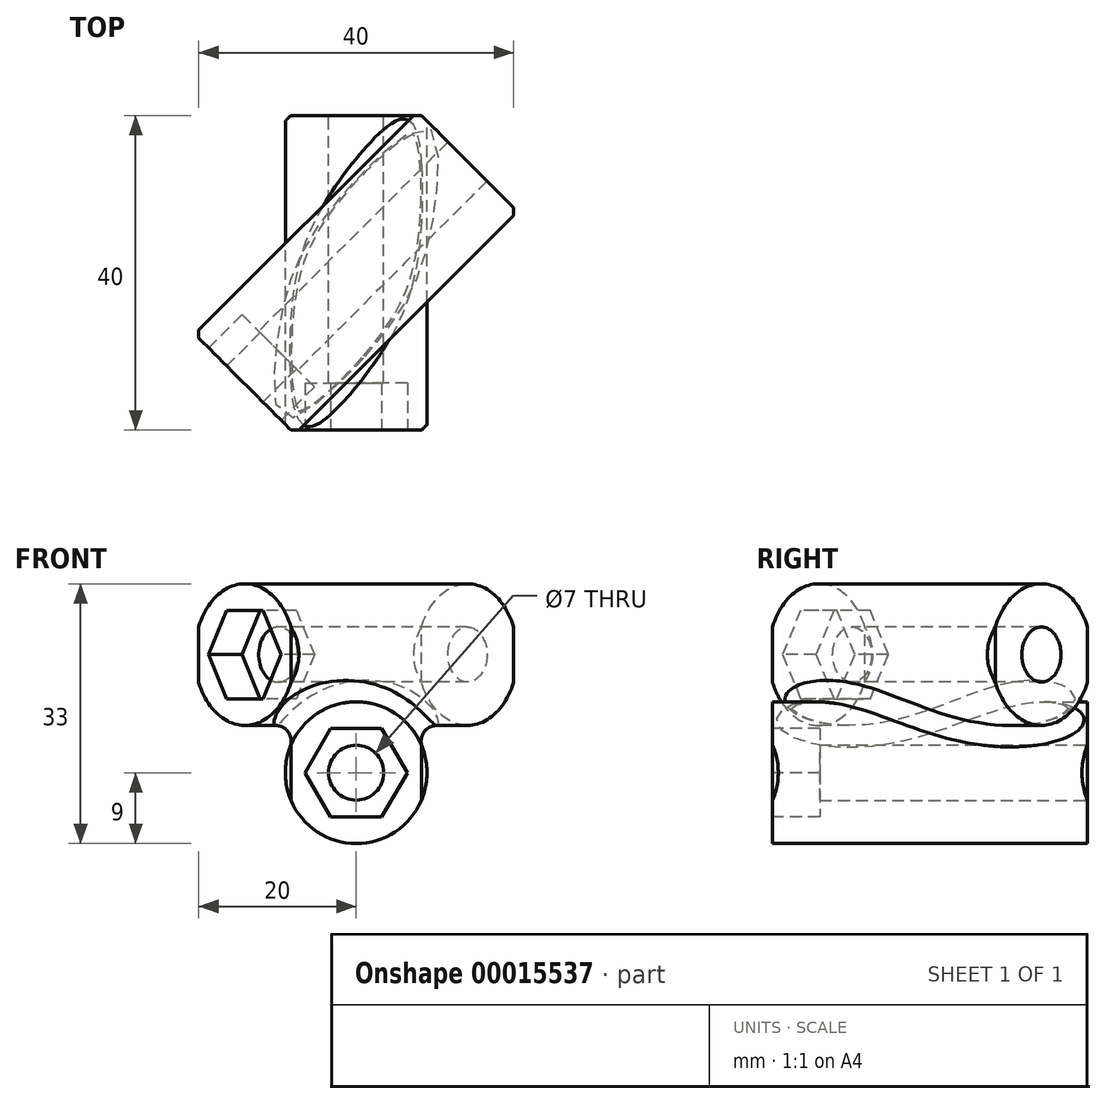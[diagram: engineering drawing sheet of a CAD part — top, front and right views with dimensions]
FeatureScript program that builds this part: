
annotation { "Feature Type Name" : "Feature", "Feature Type Description" : "" }
export const myFeature = defineFeature(function(context is Context, id is Id, definition is map)
    precondition{}
    {
        {
            var Q0;
            Q0=qCreatedBy(makeId("Top.planeOp"),FACE);
            var sketch = newSketch(context, id + "F0", { "sketchPlane" : qUnion([Q0])});
            skLineSegment(sketch, "E0.rect.bottom", {"start": v(3.5, -20) * mm, "end": v(-3.5, -20) * mm});
            skLineSegment(sketch, "E0.rect.top", {"start": v(3.5, 20) * mm, "end": v(-3.5, 20) * mm});
            skLineSegment(sketch, "E0.rect.left", {"start": v(3.5, -20) * mm, "end": v(3.5, 20) * mm});
            skLineSegment(sketch, "E0.rect.right", {"start": v(-3.5, -20) * mm, "end": v(-3.5, 20) * mm});
            skPoint(sketch, "E0.rect.middle", {"position": v(0, 0) * mm});
            skLineSegment(sketch, "E1", {"start": v(-16.62, -11.67) * mm, "end": v(11.67, 16.62) * mm});
            skLineSegment(sketch, "E2", {"start": v(11.67, 16.62) * mm, "end": v(16.62, 11.67) * mm});
            skLineSegment(sketch, "E3", {"start": v(16.62, 11.67) * mm, "end": v(-11.67, -16.62) * mm});
            skLineSegment(sketch, "E4", {"start": v(-11.67, -16.62) * mm, "end": v(-16.62, -11.67) * mm});
            skLineSegment(sketch, "E5", {"start": v(11.67, 16.62) * mm, "end": v(-11.67, -16.62) * mm, "construction": true});
            skSolve(sketch);
        }
        {
            var Q0;
            Q0=qCreatedBy(makeId("Front.planeOp"),FACE);
            var sketch = newSketch(context, id + "F1", { "sketchPlane" : qUnion([Q0])});
            skCircle(sketch, "E6", {"center": v(0, -7.5) * mm, "radius": 3.5 * mm});
            skCircle(sketch, "E7", {"center": v(0, -7.5) * mm, "radius": 9 * mm});
            skSolve(sketch);
        }
        {
            var Q0;
            Q0 = qSketchRegion(id + "F1", true);
            extrude(context, id + "F2", {"entities" : qUnion([Q0]), "depth" : 20 * mm, "hasSecondDirection" : true, "secondDirectionOppositeDirection" : true, "secondDirectionDepth" : 20 * mm});
        }
        {
            var Q0;
            Q0=sQuery(id+"F0.wireOp",EDGE,"E1");
            var Q1;
            Q1=sQuery(id+"F0.wireOp",VERTEX,"E1.start");
            cPlane(context, id + "F3", {"entities" : qUnion([Q0, Q1]), "cplaneType" : CPlaneType.LINE_POINT, "offset" : 150 * mm, "width" : 150 * mm, "height" : 150 * mm});
        }
        {
            var Q0;
            Q0=qCreatedBy(id+"F3.planeOp",FACE);
            var sketch = newSketch(context, id + "F4", { "sketchPlane" : qUnion([Q0])});
            skCircle(sketch, "E8", {"center": v(0, 7.5) * mm, "radius": 9 * mm});
            skCircle(sketch, "E9", {"center": v(0, 7.5) * mm, "radius": 3.5 * mm});
            skLineSegment(sketch, "E10", {"start": v(0, 7.5) * mm, "end": v(0, 0) * mm, "construction": true});
            skSolve(sketch);
        }
        {
            var Q0;
            Q0 = qSketchRegion(id + "F4", true);
            extrude(context, id + "F5", {"entities" : qUnion([Q0]), "operationType" : NewBodyOperationType.ADD, "depth" : 40 * mm});
        }
        {
            var Q0;
            Q0=makeQuery(id+"F2.opExtrude","CAP_FACE",FACE,{"disambiguationData":[OSD([sQuery(id+"F1.wireOp",EDGE,"E6"),sQuery(id+"F1.wireOp",EDGE,"E7")])],"isStart":false});
            var sketch = newSketch(context, id + "F6", { "sketchPlane" : qUnion([Q0])});
            skCircle(sketch, "E11.cCircle", {"center": v(0, -7.5) * mm, "radius": 6.5 * mm, "construction": true});
            skLineSegment(sketch, "E11.0", {"start": v(6.5, -7.5) * mm, "end": v(3.25, -13.13) * mm});
            skLineSegment(sketch, "E11.1", {"start": v(3.25, -13.13) * mm, "end": v(-3.25, -13.13) * mm});
            skLineSegment(sketch, "E11.2", {"start": v(-3.25, -13.13) * mm, "end": v(-6.5, -7.5) * mm});
            skLineSegment(sketch, "E11.3", {"start": v(-6.5, -7.5) * mm, "end": v(-3.25, -1.87) * mm});
            skLineSegment(sketch, "E11.4", {"start": v(-3.25, -1.87) * mm, "end": v(3.25, -1.87) * mm});
            skLineSegment(sketch, "E11.5", {"start": v(3.25, -1.87) * mm, "end": v(6.5, -7.5) * mm});
            skSolve(sketch);
        }
        {
            var Q0;
            Q0 = qSketchRegion(id + "F6", true);
            extrude(context, id + "F7", {"entities" : qUnion([Q0]), "operationType" : NewBodyOperationType.REMOVE, "oppositeDirection" : true, "depth" : 6 * mm});
        }
        {
            var Q0;
            Q0=makeQuery(id+"F5.opExtrude","CAP_FACE",FACE,{"disambiguationData":[OSD([sQuery(id+"F4.wireOp",EDGE,"E8"),sQuery(id+"F4.wireOp",EDGE,"E9")])],"isStart":true});
            var sketch = newSketch(context, id + "F8", { "sketchPlane" : qUnion([Q0])});
            skCircle(sketch, "E12.cCircle", {"center": v(0, 7.5) * mm, "radius": 6.5 * mm, "construction": true});
            skLineSegment(sketch, "E12.0", {"start": v(6.5, 7.5) * mm, "end": v(3.25, 1.87) * mm});
            skLineSegment(sketch, "E12.1", {"start": v(3.25, 1.87) * mm, "end": v(-3.25, 1.87) * mm});
            skLineSegment(sketch, "E12.2", {"start": v(-3.25, 1.87) * mm, "end": v(-6.5, 7.5) * mm});
            skLineSegment(sketch, "E12.3", {"start": v(-6.5, 7.5) * mm, "end": v(-3.25, 13.13) * mm});
            skLineSegment(sketch, "E12.4", {"start": v(-3.25, 13.13) * mm, "end": v(3.25, 13.13) * mm});
            skLineSegment(sketch, "E12.5", {"start": v(3.25, 13.13) * mm, "end": v(6.5, 7.5) * mm});
            skSolve(sketch);
        }
        {
            var Q0;
            Q0 = qSketchRegion(id + "F8", true);
            extrude(context, id + "F9", {"entities" : qUnion([Q0]), "operationType" : NewBodyOperationType.REMOVE, "oppositeDirection" : true, "depth" : 6 * mm});
        }
        {
            var Q0;
            Q0=makeQuery(id+"F5.boolean.opBoolean","INTERSECT",EDGE,{"derivedFrom":[makeQuery(id+"F2.opExtrude","SWEPT_FACE",FACE,{"disambiguationData":[OSD([sQuery(id+"F1.wireOp",EDGE,"E7")])]}),makeQuery(id+"F5.opExtrude","SWEPT_FACE",FACE,{"disambiguationData":[OSD([sQuery(id+"F4.wireOp",EDGE,"E8")])]})]});
            fillet(context, id + "F10", {"entities" : qUnion([Q0]), "radius" : 2 * mm, "tangentPropagation" : true, "allowEdgeOverflow" : false});
        }
        {
            var Q0;
            Q0=qCreatedBy(makeId("Top.planeOp"),FACE);
            var sketch = newSketch(context, id + "F11", { "sketchPlane" : qUnion([Q0])});
            skCircle(sketch, "E13.cCircle", {"center": v(0, 0) * mm, "radius": 21.65 * mm, "construction": true});
            skLineSegment(sketch, "E13.0", {"start": v(-8.28, -20) * mm, "end": v(-20, -8.28) * mm});
            skLineSegment(sketch, "E13.1", {"start": v(-20, -8.28) * mm, "end": v(-20, 8.28) * mm});
            skLineSegment(sketch, "E13.2", {"start": v(-20, 8.28) * mm, "end": v(-8.28, 20) * mm});
            skLineSegment(sketch, "E13.3", {"start": v(-8.28, 20) * mm, "end": v(8.28, 20) * mm});
            skLineSegment(sketch, "E13.4", {"start": v(8.28, 20) * mm, "end": v(20, 8.28) * mm});
            skLineSegment(sketch, "E13.5", {"start": v(20, 8.28) * mm, "end": v(20, -8.28) * mm});
            skLineSegment(sketch, "E13.6", {"start": v(20, -8.28) * mm, "end": v(8.28, -20) * mm});
            skLineSegment(sketch, "E13.7", {"start": v(8.28, -20) * mm, "end": v(-8.28, -20) * mm});
            skSolve(sketch);
        }
        {
            var Q0;
            Q0 = qSketchRegion(id + "F11", true);
            extrude(context, id + "F12", {"entities" : qUnion([Q0]), "operationType" : NewBodyOperationType.INTERSECT, "oppositeDirection" : true, "depth" : 25 * mm, "hasSecondDirection" : true, "secondDirectionOppositeDirection" : false, "secondDirectionDepth" : 25 * mm});
        }
    });
